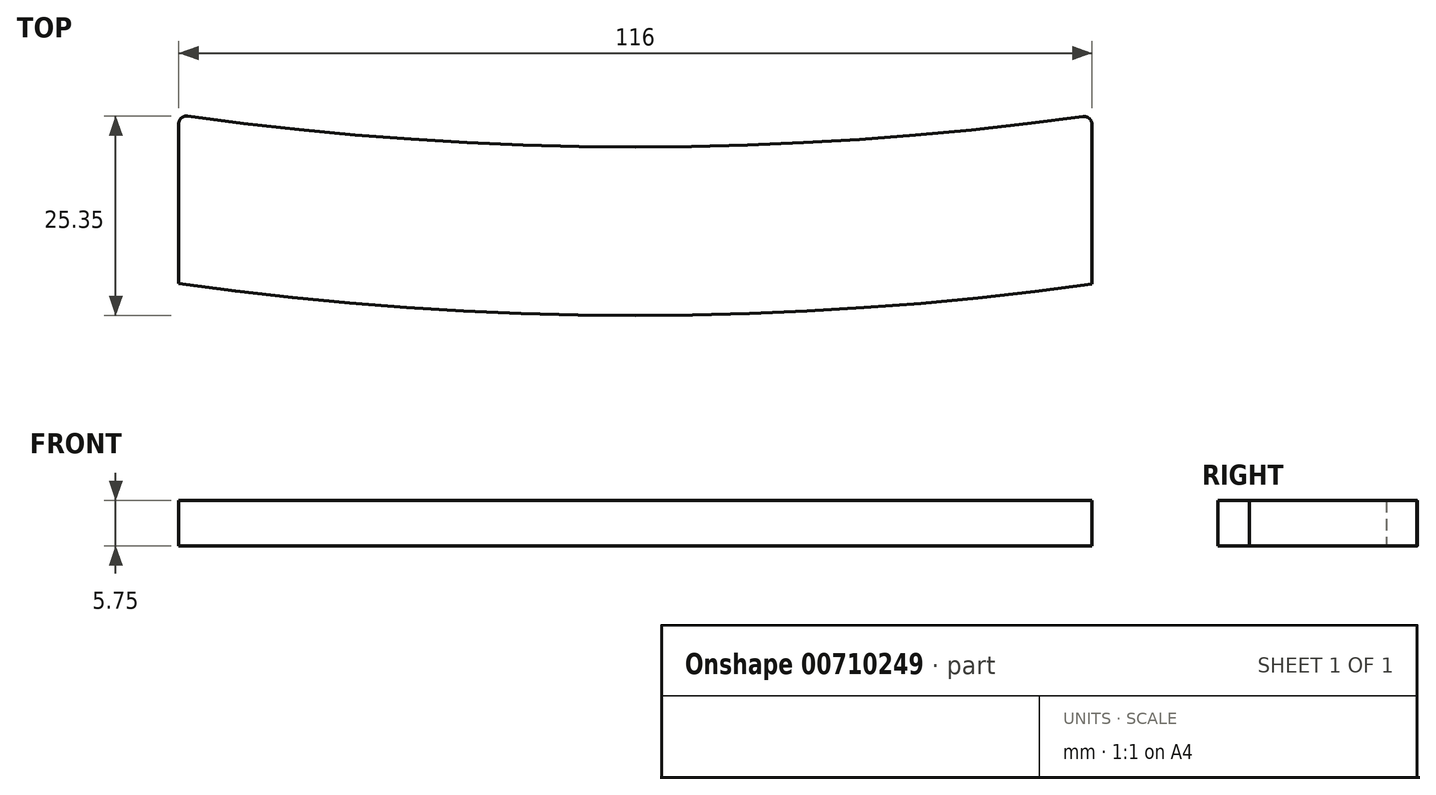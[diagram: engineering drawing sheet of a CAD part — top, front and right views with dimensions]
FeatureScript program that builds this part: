
annotation { "Feature Type Name" : "Feature", "Feature Type Description" : "" }
export const myFeature = defineFeature(function(context is Context, id is Id, definition is map)
    precondition{}
    {
        {
            var Q0;
            Q0=qCreatedBy(makeId("Top.planeOp"),FACE);
            var sketch = newSketch(context, id + "F0", { "sketchPlane" : qUnion([Q0])});
            skArc(sketch, "E0", {"start": v(76, 16.23) * mm, "mid": v(75.64, 17) * mm, "end": v(74.82, 17.22) * mm});
            skArc(sketch, "E1", {"start": v(-74.82, 17.29) * mm, "mid": v(-75.64, 17.07) * mm, "end": v(-76, 16.3) * mm});
            skLineSegment(sketch, "E2", {"start": v(-55.5, 7.05) * mm, "end": v(-55.5, -13.23) * mm});
            skArc(sketch, "E3", {"start": v(-55.5, -13.23) * mm, "mid": v(2.5, -17.3) * mm, "end": v(60.5, -13.28) * mm});
            skLineSegment(sketch, "E4", {"start": v(60.5, -13.28) * mm, "end": v(60.5, 7) * mm});
            skArc(sketch, "E5", {"start": v(60.5, 7) * mm, "mid": v(60.16, 7.75) * mm, "end": v(59.36, 7.98) * mm});
            skArc(sketch, "E6", {"start": v(-54.36, 8.04) * mm, "mid": v(2.5, 4.12) * mm, "end": v(59.36, 7.98) * mm});
            skArc(sketch, "E7", {"start": v(-54.36, 8.04) * mm, "mid": v(-55.16, 7.8) * mm, "end": v(-55.5, 7.05) * mm});
            skSolve(sketch);
        }
        {
            var Q0;
            Q0=makeQuery(id+"F0.imprint","IMPRINT",FACE,{"disambiguationData":[TD([[makeQuery(id+"F0.imprint","IMPRINT",EDGE,{"derivedFrom":sQuery(id+"F0.wireOp",EDGE,"E2")}),1.0]])]});
            extrude(context, id + "F1", {"entities" : qUnion([Q0]), "depth" : 5.75 * mm, "offsetDistance" : 25 * mm});
        }
    });
